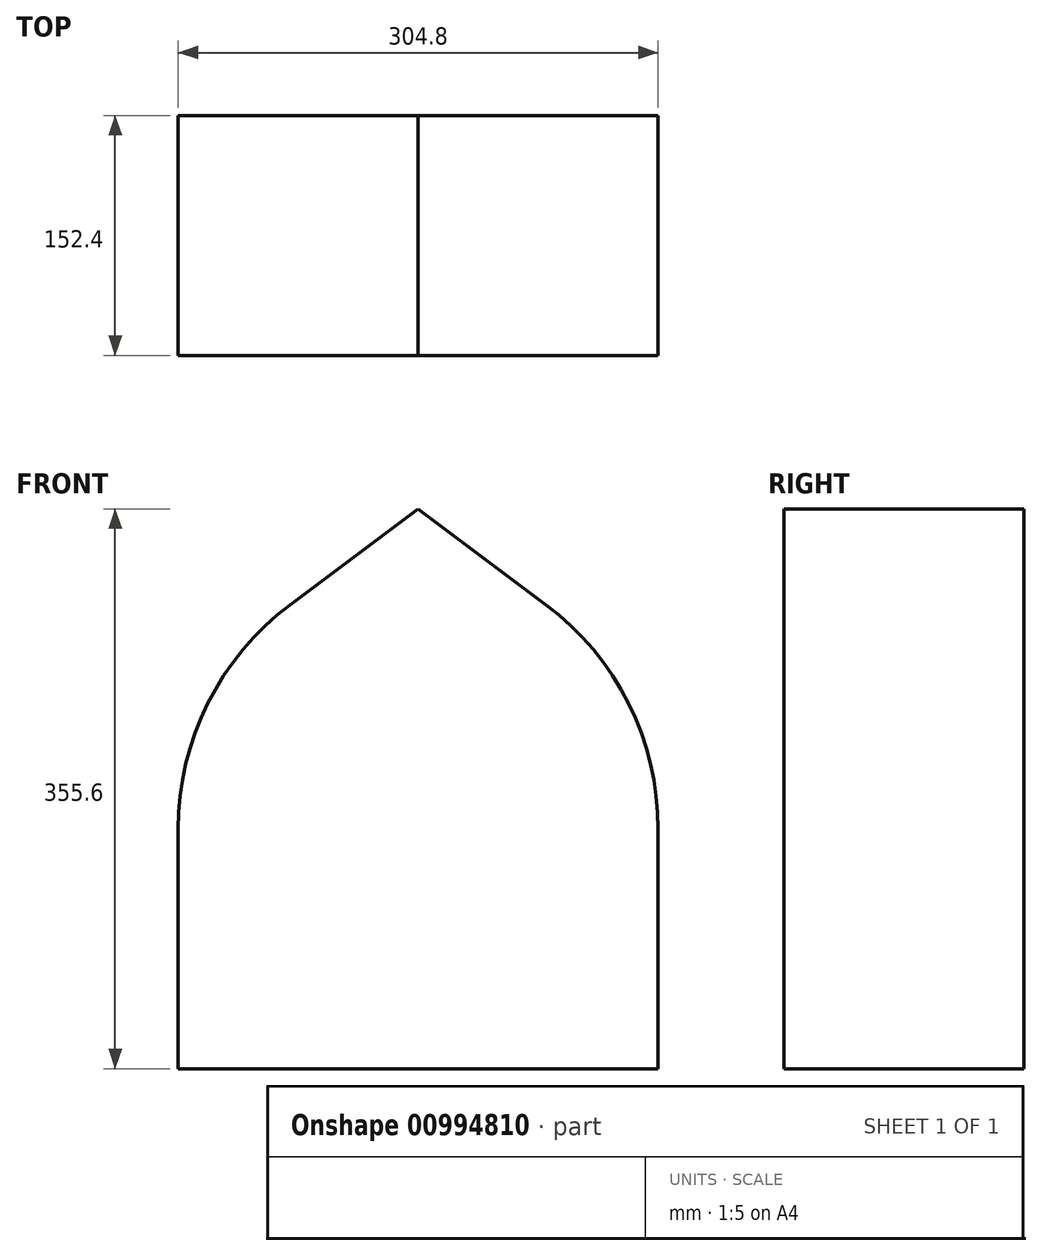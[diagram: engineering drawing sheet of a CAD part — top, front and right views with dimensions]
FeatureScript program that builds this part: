
annotation { "Feature Type Name" : "Feature", "Feature Type Description" : "" }
export const myFeature = defineFeature(function(context is Context, id is Id, definition is map)
    precondition{}
    {
        {
            var Q0;
            Q0=qCreatedBy(makeId("Front.planeOp"),FACE);
            var sketch = newSketch(context, id + "F0", { "sketchPlane" : qUnion([Q0])});
            skLineSegment(sketch, "E0", {"start": v(-152.4, 0) * mm, "end": v(152.4, 0) * mm});
            skLineSegment(sketch, "E1", {"start": v(-152.4, 0) * mm, "end": v(-152.4, 152.4) * mm});
            skLineSegment(sketch, "E2", {"start": v(152.4, 0) * mm, "end": v(152.4, 152.4) * mm});
            skArc(sketch, "E3", {"start": v(-152.4, 152.4) * mm, "mid": v(-133.63, 231.91) * mm, "end": v(-81.28, 294.64) * mm});
            skArc(sketch, "E4.MirrorCS", {"start": v(152.4, 152.4) * mm, "mid": v(133.63, 231.91) * mm, "end": v(81.28, 294.64) * mm});
            skLineSegment(sketch, "E5", {"start": v(-81.28, 294.64) * mm, "end": v(0, 355.6) * mm});
            skLineSegment(sketch, "E6.MirrorCS", {"start": v(81.28, 294.64) * mm, "end": v(0, 355.6) * mm});
            skSolve(sketch);
        }
        {
            var Q0;
            Q0=makeQuery(id+"F0.imprint","IMPRINT",FACE,{"disambiguationData":[TD([[makeQuery(id+"F0.imprint","IMPRINT",EDGE,{"derivedFrom":sQuery(id+"F0.wireOp",EDGE,"E0")}),1.0]])]});
            extrude(context, id + "F1", {"entities" : qUnion([Q0]), "depth" : 152.4 * mm, "offsetDistance" : 25.4 * mm});
        }
    });
